# Revit family: Hager-Mini_Gamma-IP30-sistema-NoHosted-PT-pt
name_source: partatom
category: Electrical Equipment
units: mm (PartAtom-declared; Revit-internal decimal feet)

## family parameters
Always vertical = Yes
Cut with Voids When Loaded = No
Panel Configuration = Two Columns, Circuits Across
Part Type = Panelboard
Room Calculation Point = No
Round Connector Dimension = Use Diameter
Shared = No
Work Plane-Based = Yes

## types (5) — shared parameters
Default Elevation = 1219 mm
EF000003 - Método de montagem = EV000384 - Montagem em superfície (gesso)
EF000007 - Cor = EV000202 - Branco
EF000049 - Profundidade = 82 mm  [stored 0.269029 ft]
EF000116 - Número RAL = 9010
EF000118 - Com tampa de montagem = No
EF000266 - Número de linhas = 1
EF000339 - Tipo de difusor = EV005746 - Opcional
EF001062 - Versão EMC = No
EF001131 - Profundidade interior = 82 mm  [stored 0.269029 ft]
EF001134 - Calha DIN = No
EF001596 - Material do corpo = EV000139 - Plástico
EF004462 - Tipo de fecho = EV000154 - Outro
EF005474 - Grau de proteção (IP) = EV006410 - IP30
EF006244 - Tampa/porta transparente = No
EF006306 - Com fecho = No
EF009212 - Tipo de tampa = EV009916 - Com recuo
EF015941 - Porta para passagem de sinal = No
HG000001 - Número de colunas = 1
HG000002 - Com porta ou tampa = No
HG000003 - Gama = Mini gamma
HG000005 - Espessura = 3 mm  [stored 0.00984252 ft]
HG000006 - Encastrado = No
HG000009 - Porta dupla = No
HG000010 - Portas assimétricas = No
HG000011 - Filas vazias desde da parte de baixo = No
HG000017 - Distância entre polos = 18 mm  [stored 0.0590551 ft]
Manufacturer = Hager
Type Comments = Mini gamma
zero-valued in all types: EF000218 - Profundidade incorporada, EF000332 - Altura embutida, EF000846 - Largura para embutir, HG000007 - Número de colunas vazias, HG000008 - Número de filas vazias

## per-type parameters (varying)
| type | EF000008 - Largura | EF000040 - Altura | EF001088 - Extensão possível | EF002950 - Largura em número de módulos | EF015776 - Borne de terra | EF015777 - Borne de neutro | HG000004 - Referência do Fabricante | Model |
| Montagem em superfície IP30 L110 A180 P82 4 unidade de divisão - GD104B | 110 mm | 180 mm | No | 4 | No | No | GD104B | GD104B |
| Montagem em superfície IP30 L146 A180 P82 6 unidade de divisão - GD106N | 146 mm | 180 mm | Yes | 6 | Yes | Yes | GD106N | GD106N |
| Montagem em superfície IP30 L182 A180 P82 8 unidade de divisão - GD108N | 182 mm | 180 mm | Yes | 8 | Yes | Yes | GD108N | GD108N |
| Montagem em superfície IP30 L218 A180 P82 10 unidade de divisão - GD110N | 218 mm | 180 mm | Yes | 10 | Yes | Yes | GD110N | GD110N |
| Montagem em superfície IP30 L55 A160 P82 2 unidade de divisão - GD102B | 55 mm  [stored 0.180446 ft] | 160 mm  [stored 0.524934 ft] | No | 2 | No | No | GD102B | GD102B |

note: [stored X ft] marks values corroborated as IEEE doubles in the binary element streams (Revit-internal decimal feet)

## geometry (parser evidence)
native form markers: Sweep x13
no freeform markers — native parametric forms only
